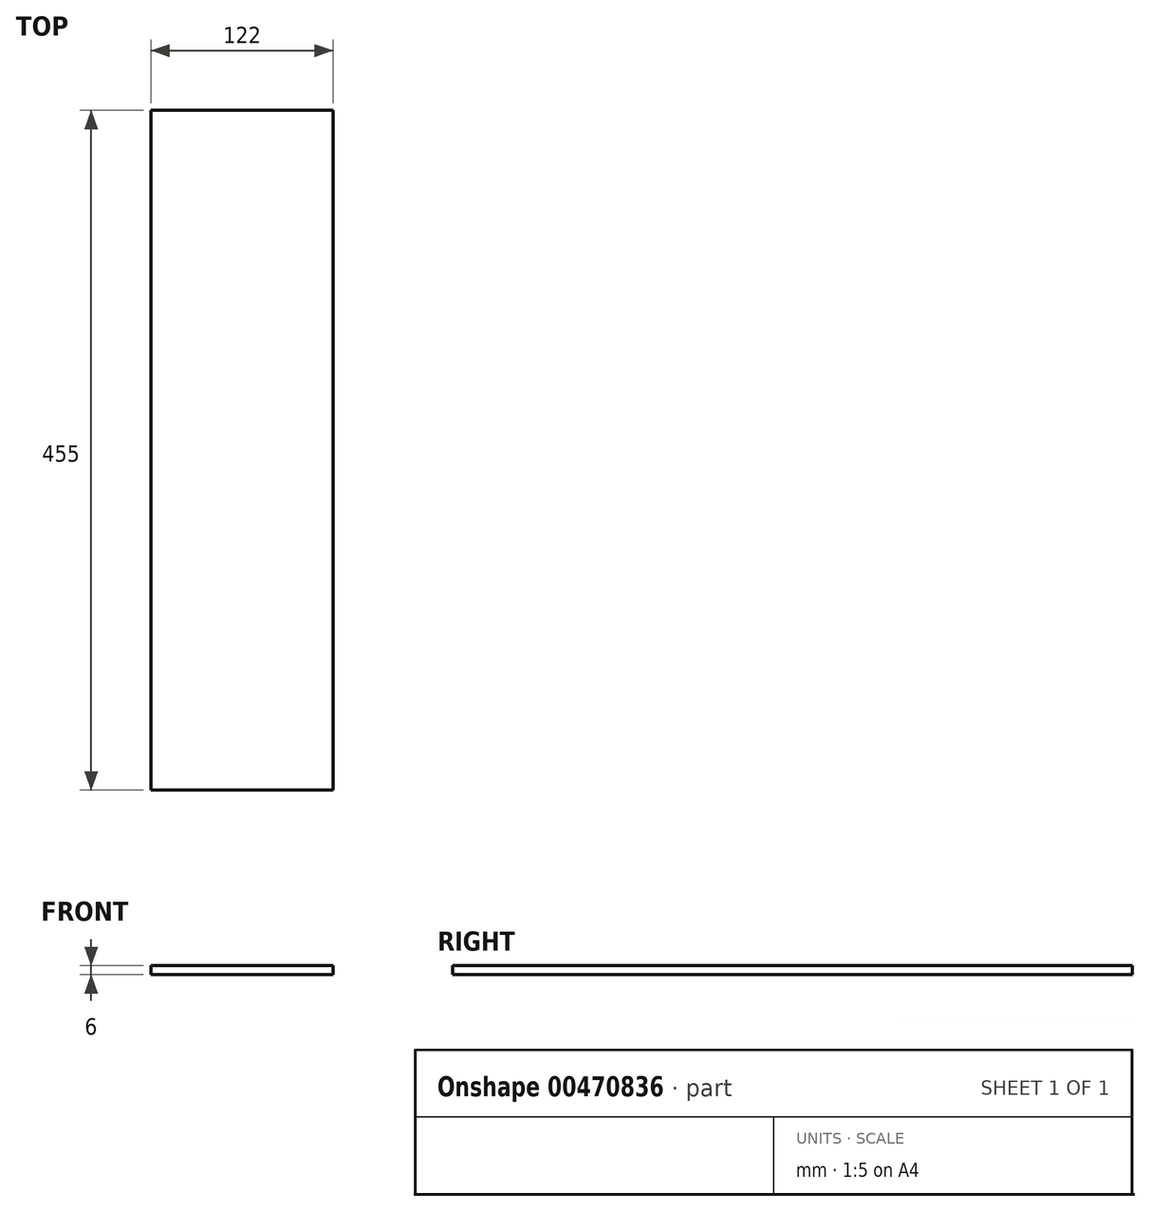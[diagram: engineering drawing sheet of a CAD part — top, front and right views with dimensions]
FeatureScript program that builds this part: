
annotation { "Feature Type Name" : "Feature", "Feature Type Description" : "" }
export const myFeature = defineFeature(function(context is Context, id is Id, definition is map)
    precondition{}
    {
        {
            var Q0;
            Q0=qCreatedBy(makeId("Top.planeOp"),FACE);
            var sketch = newSketch(context, id + "F0", { "sketchPlane" : qUnion([Q0])});
            skLineSegment(sketch, "E0.bottom", {"start": v(-15.9, 414.44) * mm, "end": v(106.1, 414.44) * mm});
            skLineSegment(sketch, "E0.top", {"start": v(-15.9, -40.56) * mm, "end": v(106.1, -40.56) * mm});
            skLineSegment(sketch, "E0.left", {"start": v(-15.9, 414.44) * mm, "end": v(-15.9, -40.56) * mm});
            skLineSegment(sketch, "E0.right", {"start": v(106.1, 414.44) * mm, "end": v(106.1, -40.56) * mm});
            skSolve(sketch);
        }
        {
            var Q0;
            Q0=makeQuery(id+"F0.imprint","IMPRINT",FACE,{"disambiguationData":[TD([[makeQuery(id+"F0.imprint","IMPRINT",EDGE,{"derivedFrom":sQuery(id+"F0.wireOp",EDGE,"E0.bottom")}),-1.0]])]});
            extrude(context, id + "F1", {"entities" : qUnion([Q0]), "depth" : 6 * mm});
        }
    });
